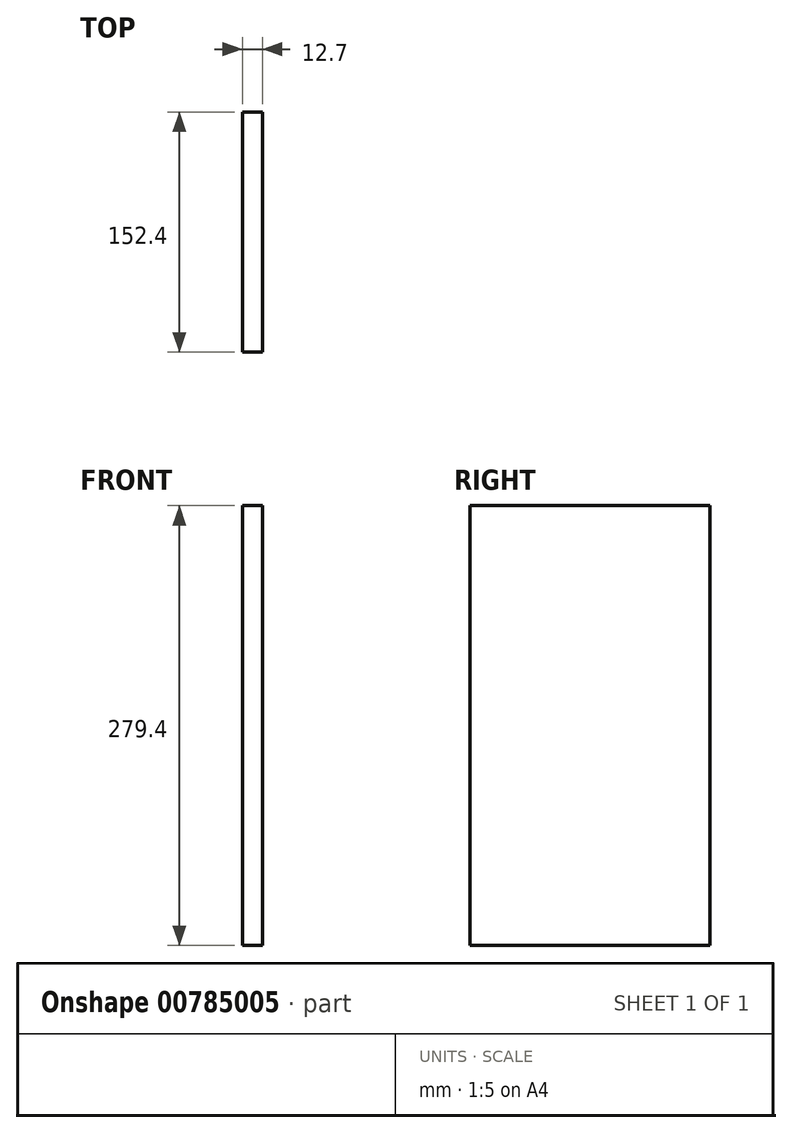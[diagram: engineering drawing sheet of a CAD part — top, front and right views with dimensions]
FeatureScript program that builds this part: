
annotation { "Feature Type Name" : "Feature", "Feature Type Description" : "" }
export const myFeature = defineFeature(function(context is Context, id is Id, definition is map)
    precondition{}
    {
        {
            var Q0;
            Q0=qCreatedBy(makeId("Right.planeOp"),FACE);
            var sketch = newSketch(context, id + "F0", { "sketchPlane" : qUnion([Q0])});
            skLineSegment(sketch, "E0.bottom", {"start": v(-76.2, 139.7) * mm, "end": v(76.2, 139.7) * mm});
            skLineSegment(sketch, "E0.top", {"start": v(-76.2, -139.7) * mm, "end": v(76.2, -139.7) * mm});
            skLineSegment(sketch, "E0.left", {"start": v(-76.2, 139.7) * mm, "end": v(-76.2, -139.7) * mm});
            skLineSegment(sketch, "E0.right", {"start": v(76.2, 139.7) * mm, "end": v(76.2, -139.7) * mm});
            skPoint(sketch, "E0.middle", {"position": v(0, 0) * mm});
            skSolve(sketch);
        }
        {
            var Q0;
            Q0=makeQuery(id+"F0.imprint","IMPRINT",FACE,{"disambiguationData":[TD([[makeQuery(id+"F0.imprint","IMPRINT",EDGE,{"derivedFrom":sQuery(id+"F0.wireOp",EDGE,"E0.bottom")}),-1.0]])]});
            extrude(context, id + "F1", {"entities" : qUnion([Q0]), "depth" : 12.7 * mm, "offsetDistance" : 25.4 * mm});
        }
    });
